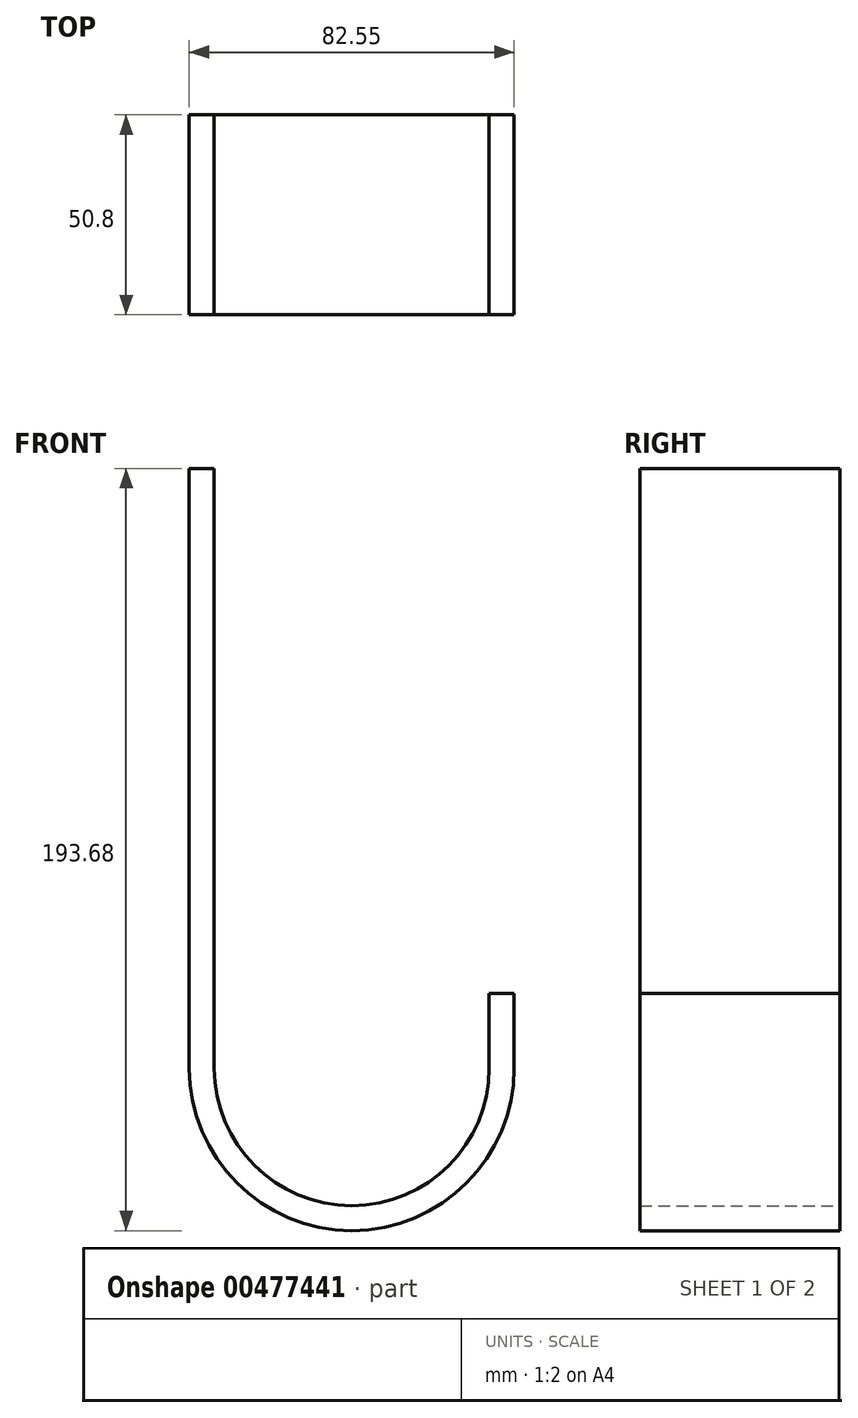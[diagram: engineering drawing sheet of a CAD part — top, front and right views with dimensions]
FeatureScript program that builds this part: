
annotation { "Feature Type Name" : "Feature", "Feature Type Description" : "" }
export const myFeature = defineFeature(function(context is Context, id is Id, definition is map)
    precondition{}
    {
        {
            var Q0;
            Q0=qCreatedBy(makeId("Front.planeOp"),FACE);
            var sketch = newSketch(context, id + "F0", { "sketchPlane" : qUnion([Q0])});
            skLineSegment(sketch, "E0", {"start": v(0, 0) * mm, "end": v(0, 152.4) * mm});
            skLineSegment(sketch, "E1", {"start": v(0, 152.4) * mm, "end": v(6.35, 152.4) * mm});
            skLineSegment(sketch, "E2", {"start": v(6.35, 152.4) * mm, "end": v(6.35, 0) * mm});
            skArc(sketch, "E3", {"start": v(6.35, 0) * mm, "mid": v(41.28, -34.93) * mm, "end": v(76.2, 0) * mm});
            skArc(sketch, "E4", {"start": v(0, 0) * mm, "mid": v(41.28, -41.27) * mm, "end": v(82.55, 0) * mm});
            skLineSegment(sketch, "E5", {"start": v(76.2, 0) * mm, "end": v(76.2, 19.05) * mm});
            skLineSegment(sketch, "E6", {"start": v(76.2, 19.05) * mm, "end": v(82.55, 19.05) * mm});
            skLineSegment(sketch, "E7", {"start": v(82.55, 19.05) * mm, "end": v(82.55, 0) * mm});
            skSolve(sketch);
        }
        {
            var Q0;
            Q0=makeQuery(id+"F0.imprint","IMPRINT",FACE,{"disambiguationData":[TD([[makeQuery(id+"F0.imprint","IMPRINT",EDGE,{"derivedFrom":sQuery(id+"F0.wireOp",EDGE,"E0")}),-1.0]])]});
            extrude(context, id + "F1", {"entities" : qUnion([Q0]), "depth" : 50.8 * mm});
        }
    });
